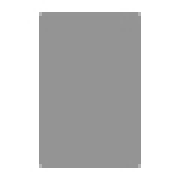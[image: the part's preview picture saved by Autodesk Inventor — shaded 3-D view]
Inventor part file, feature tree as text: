
AUTODESK INVENTOR PART (.ipt)
format: ipt  version: 2025 (Build 290162010, 162A)  size: 187,904 bytes
history: native  units: mm
features: sketch x5, reference x4, other x4, hole x3, extrude x2, fillet x2, chamfer x1
ambient origin geometry x8: Origin, YZ Plane, XZ Plane, XY Plane, X Axis, Y Axis, Z Axis, Center Point
bodies: Solid1 (feature_tree)
feature tree (21):
  extrude  "Extrusion1"  Depth=12.0mm
  fillet  "Fillet1"  Radius=200.0mm
  chamfer  "Chamfer1"  [1 undecoded]
  sketch  "Skizze2"  dims[d3=100.0mm]
  hole  "Bohrung1"  [1 undecoded]
  hole  "Bohrung2"  [1 undecoded]
  hole  "Bohrung3"  [1 undecoded]
  extrude  "Extrusion2"  Depth=3.0mm
  fillet  "Rundung2"  Radius=70.0mm
  sketch  "Sketch1"  dims[d0=24.0mm d1=12.0mm d2=200.0mm]
  sketch  "Skizze3"  dims[d4=8.0mm]
  sketch  "Skizze4"  dims[d5=0.0mm]
  reference  "Referenz1"
  reference  "Referenz2"
  reference  "Referenz3"
  reference  "Referenz4"
  sketch  "Skizze5"  dims[d6=0.0mm d7=0.0mm d8=0.0mm d9=2.0mm d10=45.0deg d11=0.0mm d12=15.0mm d13=70.0mm d14=5.3mm d15=6.0mm d16=15.0mm d17=1.0mm d18=90.0deg d19=8.0mm d20=20.594885mm d21=4.134mm d22=10.0mm d23=6.3mm d24=2.0mm d25=90.0deg d26=8.0mm d27=20.594885mm d28=2.459mm d29=5.0mm d30=4.0mm d31=2.0mm d32=90.0deg d33=8.0mm d34=20.594885mm d35=50.0mm d36=12.0mm d37=0.0mm d38=0.0mm d39=3.0mm]
  other  "<userpath>\GIT\HDVKBM\CAD\Krandemonstrator\Demonstrator.iam"
  other  "Demonstrator.iam"
  other  "MontageAufnahmeLO:2"
  other  "MontageAufnahmeLO-LH:2"
note: 4 required parameter values undecoded (feature->parameter linkage not recoverable at this tier; creation-order binding heuristic only, values carry confidence <= 0.55)
